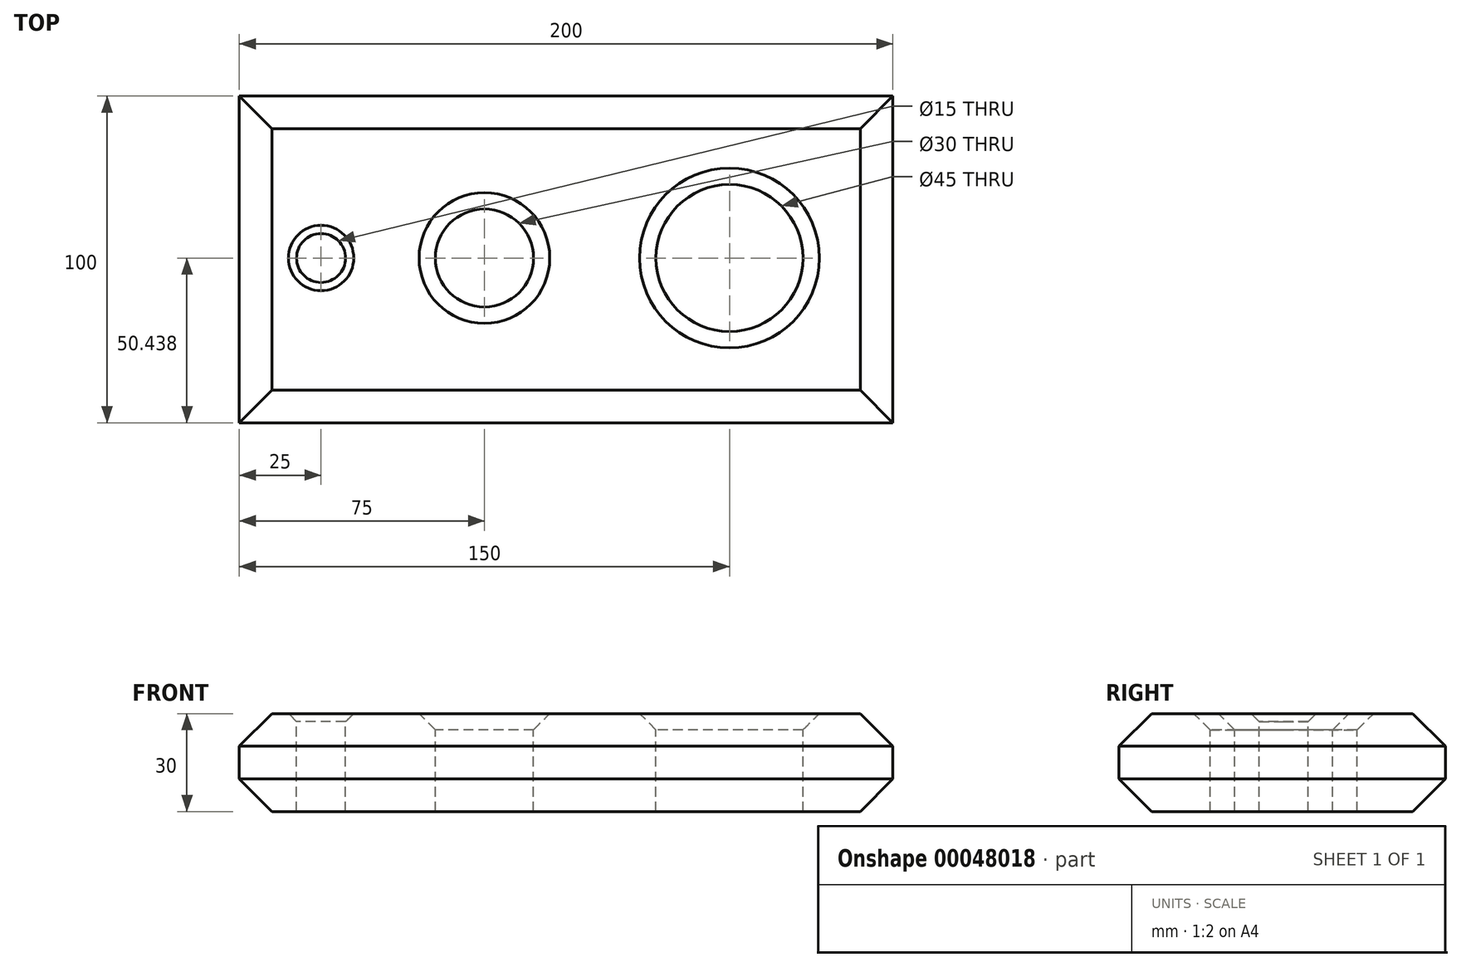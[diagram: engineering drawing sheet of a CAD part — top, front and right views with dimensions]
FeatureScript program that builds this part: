
annotation { "Feature Type Name" : "Feature", "Feature Type Description" : "" }
export const myFeature = defineFeature(function(context is Context, id is Id, definition is map)
    precondition{}
    {
        {
            var Q0;
            Q0=qCreatedBy(makeId("Top.planeOp"),FACE);
            var sketch = newSketch(context, id + "F0", { "sketchPlane" : qUnion([Q0])});
            skLineSegment(sketch, "E0.bottom", {"start": v(0, 0) * mm, "end": v(200, 0) * mm});
            skLineSegment(sketch, "E0.top", {"start": v(0, 100) * mm, "end": v(200, 100) * mm});
            skLineSegment(sketch, "E0.left", {"start": v(0, 0) * mm, "end": v(0, 100) * mm});
            skLineSegment(sketch, "E0.right", {"start": v(200, 0) * mm, "end": v(200, 100) * mm});
            skPoint(sketch, "E1", {"position": v(25, 50.44) * mm});
            skPoint(sketch, "E2", {"position": v(75, 50.44) * mm});
            skPoint(sketch, "E3", {"position": v(150, 50.44) * mm});
            skSolve(sketch);
        }
        {
            var Q0;
            Q0 = qSketchRegion(id + "F0", true);
            extrude(context, id + "F1", {"entities" : qUnion([Q0]), "oppositeDirection" : true, "depth" : 30 * mm});
        }
        {
            var Q0;
            Q0=sQuery(id+"F0.wireOp",VERTEX,"E1");
            var Q1;
            Q1=makeQuery(id+"F1.opExtrude","SWEPT_BODY",BODY,{"disambiguationData":[OSD([sQuery(id+"F0.wireOp",EDGE,"E0.bottom"),sQuery(id+"F0.wireOp",EDGE,"E0.top"),sQuery(id+"F0.wireOp",EDGE,"E0.left"),sQuery(id+"F0.wireOp",EDGE,"E0.right")])]});
            hole(context, id + "F2", {"style" : HoleStyle.C_SINK, "holeDiameter" : 15 * mm, "cSinkDiameter" : 20 * mm, "endStyle" : HoleEndStyle.THROUGH, "locations" : qUnion([Q0]), "scope" : qUnion([Q1]), "cSinkAngle" : 90 * degree});
        }
        {
            var Q0;
            Q0=sQuery(id+"F0.wireOp",VERTEX,"E2");
            var Q1;
            Q1=makeQuery(id+"F1.opExtrude","SWEPT_BODY",BODY,{"disambiguationData":[OSD([sQuery(id+"F0.wireOp",EDGE,"E0.bottom"),sQuery(id+"F0.wireOp",EDGE,"E0.top"),sQuery(id+"F0.wireOp",EDGE,"E0.left"),sQuery(id+"F0.wireOp",EDGE,"E0.right")])]});
            hole(context, id + "F3", {"style" : HoleStyle.C_SINK, "holeDiameter" : 30 * mm, "cSinkDiameter" : 40 * mm, "endStyle" : HoleEndStyle.THROUGH, "locations" : qUnion([Q0]), "scope" : qUnion([Q1]), "cSinkAngle" : 90 * degree});
        }
        {
            var Q0;
            Q0=sQuery(id+"F0.wireOp",VERTEX,"E3");
            var Q1;
            Q1=makeQuery(id+"F1.opExtrude","SWEPT_BODY",BODY,{"disambiguationData":[OSD([sQuery(id+"F0.wireOp",EDGE,"E0.bottom"),sQuery(id+"F0.wireOp",EDGE,"E0.top"),sQuery(id+"F0.wireOp",EDGE,"E0.left"),sQuery(id+"F0.wireOp",EDGE,"E0.right")])]});
            hole(context, id + "F4", {"style" : HoleStyle.C_SINK, "holeDiameter" : 45 * mm, "cSinkDiameter" : 55 * mm, "endStyle" : HoleEndStyle.THROUGH, "locations" : qUnion([Q0]), "scope" : qUnion([Q1]), "cSinkAngle" : 90 * degree});
        }
        {
            var Q0;
            Q0=makeQuery(id+"F1.opExtrude","CAP_EDGE",EDGE,{"disambiguationData":[OSD([sQuery(id+"F0.wireOp",EDGE,"E0.right")])],"isStart":true});
            var Q1;
            Q1=makeQuery(id+"F1.opExtrude","CAP_EDGE",EDGE,{"disambiguationData":[OSD([sQuery(id+"F0.wireOp",EDGE,"E0.right")])],"isStart":false});
            var Q2;
            Q2=makeQuery(id+"F1.opExtrude","CAP_EDGE",EDGE,{"disambiguationData":[OSD([sQuery(id+"F0.wireOp",EDGE,"E0.left")])],"isStart":true});
            var Q3;
            Q3=makeQuery(id+"F1.opExtrude","CAP_EDGE",EDGE,{"disambiguationData":[OSD([sQuery(id+"F0.wireOp",EDGE,"E0.left")])],"isStart":false});
            var Q4;
            Q4=makeQuery(id+"F1.opExtrude","CAP_EDGE",EDGE,{"disambiguationData":[OSD([sQuery(id+"F0.wireOp",EDGE,"E0.top")])],"isStart":true});
            var Q5;
            Q5=makeQuery(id+"F1.opExtrude","CAP_EDGE",EDGE,{"disambiguationData":[OSD([sQuery(id+"F0.wireOp",EDGE,"E0.top")])],"isStart":false});
            var Q6;
            Q6=makeQuery(id+"F1.opExtrude","CAP_EDGE",EDGE,{"disambiguationData":[OSD([sQuery(id+"F0.wireOp",EDGE,"E0.bottom")])],"isStart":true});
            var Q7;
            Q7=makeQuery(id+"F1.opExtrude","CAP_EDGE",EDGE,{"disambiguationData":[OSD([sQuery(id+"F0.wireOp",EDGE,"E0.bottom")])],"isStart":false});
            chamfer(context, id + "F5", {"entities" : qUnion([Q0, Q1, Q2, Q3, Q4, Q5, Q6, Q7]), "width" : 10 * mm, "tangentPropagation" : true});
        }
    });
